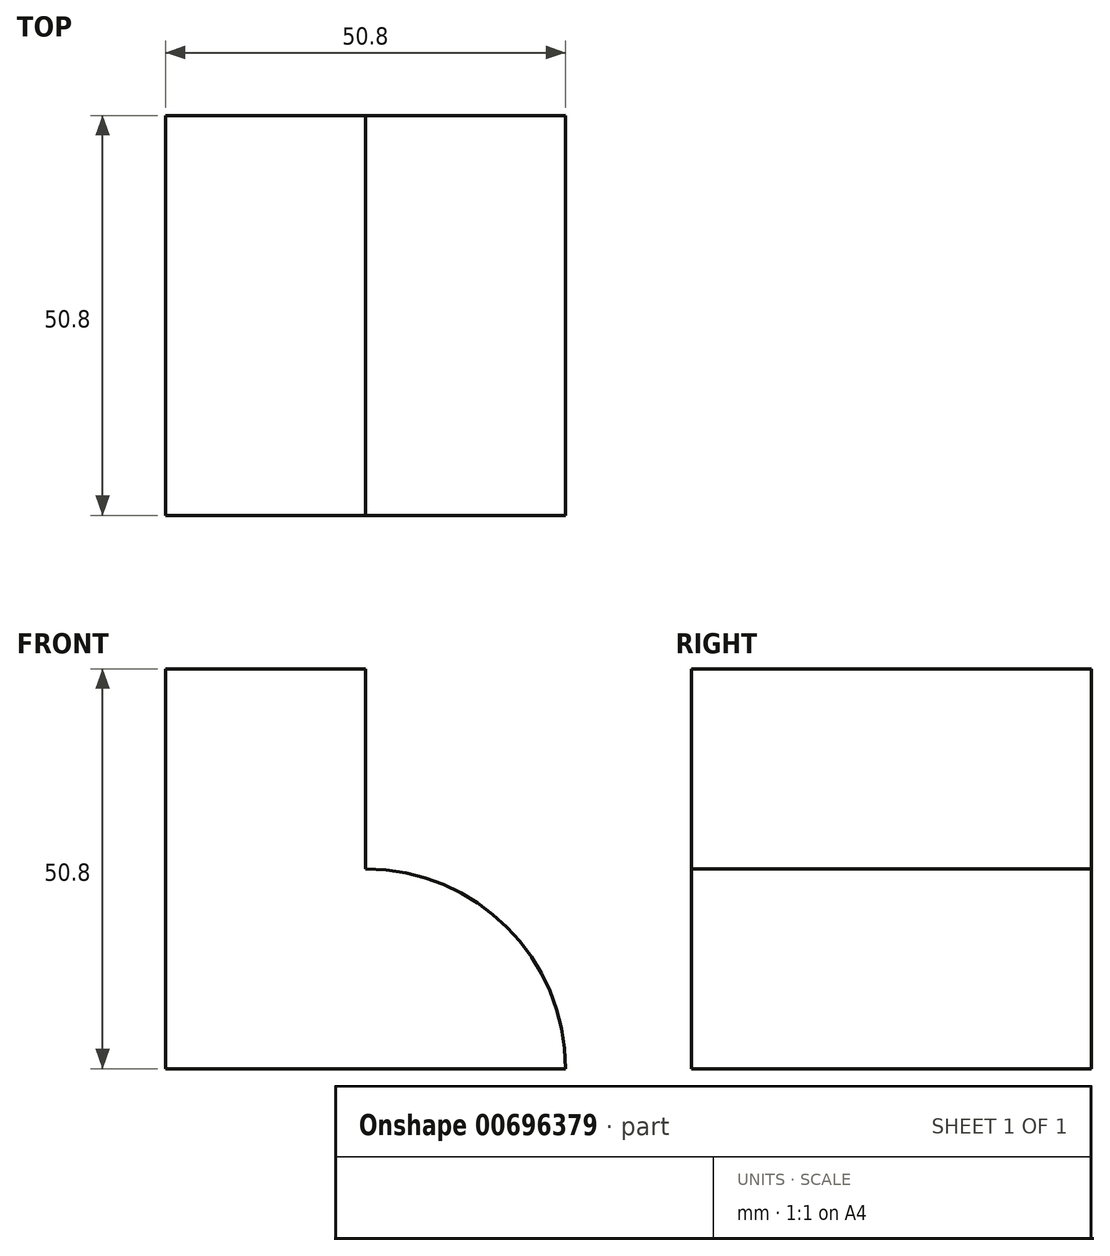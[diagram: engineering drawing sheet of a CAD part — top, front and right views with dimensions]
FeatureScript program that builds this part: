
annotation { "Feature Type Name" : "Feature", "Feature Type Description" : "" }
export const myFeature = defineFeature(function(context is Context, id is Id, definition is map)
    precondition{}
    {
        {
            var Q0;
            Q0=qCreatedBy(makeId("Front.planeOp"),FACE);
            var sketch = newSketch(context, id + "F0", { "sketchPlane" : qUnion([Q0])});
            skLineSegment(sketch, "E0.bottom", {"start": v(0, 0) * mm, "end": v(-50.8, 0) * mm});
            skLineSegment(sketch, "E0.top", {"start": v(-25.4, 50.8) * mm, "end": v(-50.8, 50.8) * mm});
            skLineSegment(sketch, "E0.left", {"start": v(0, 0) * mm, "end": v(0, 50.8) * mm});
            skLineSegment(sketch, "E0.right", {"start": v(-50.8, 0) * mm, "end": v(-50.8, 50.8) * mm});
            skLineSegment(sketch, "E1", {"start": v(-25.4, 50.8) * mm, "end": v(-25.4, 25.4) * mm});
            skPoint(sketch, "E1.endSnap0", {"position": v(0, 25.4) * mm});
            skArc(sketch, "E2", {"start": v(0, 0) * mm, "mid": v(-7.44, 17.96) * mm, "end": v(-25.4, 25.4) * mm});
            skSolve(sketch);
        }
        {
            var Q0;
            Q0 = qSketchRegion(id + "F0", true);
            extrude(context, id + "F1", {"entities" : qUnion([Q0]), "depth" : 50.8 * mm, "offsetDistance" : 25.4 * mm});
        }
    });
